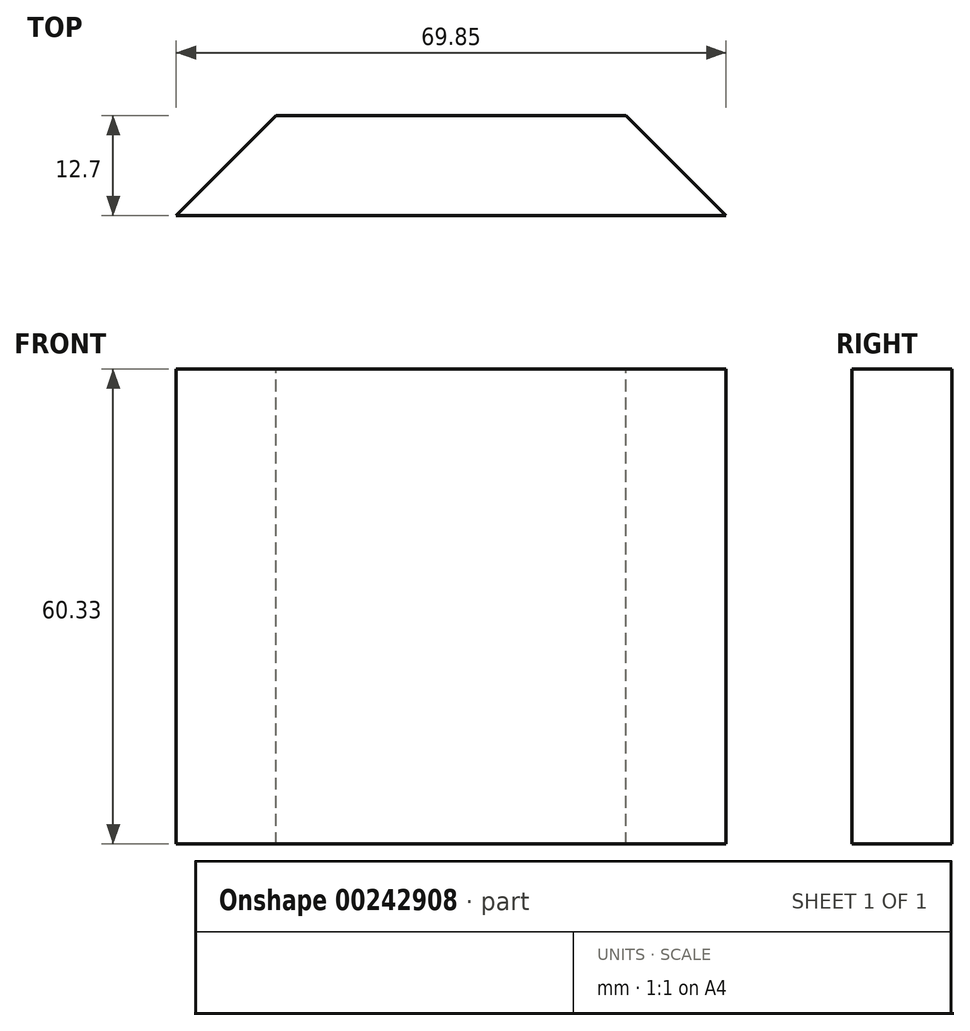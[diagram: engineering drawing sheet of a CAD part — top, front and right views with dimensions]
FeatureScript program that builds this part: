
annotation { "Feature Type Name" : "Feature", "Feature Type Description" : "" }
export const myFeature = defineFeature(function(context is Context, id is Id, definition is map)
    precondition{}
    {
        {
            var Q0;
            Q0=qCreatedBy(makeId("Front.planeOp"),FACE);
            var sketch = newSketch(context, id + "F0", { "sketchPlane" : qUnion([Q0])});
            skLineSegment(sketch, "E0", {"start": v(0, 0) * mm, "end": v(0, 60.33) * mm});
            skLineSegment(sketch, "E1", {"start": v(0, 60.33) * mm, "end": v(69.85, 60.33) * mm});
            skLineSegment(sketch, "E2", {"start": v(69.85, 60.33) * mm, "end": v(69.85, 0) * mm});
            skLineSegment(sketch, "E3", {"start": v(69.85, 0) * mm, "end": v(0, 0) * mm});
            skSolve(sketch);
        }
        {
            var Q0;
            Q0=makeQuery(id+"F0.imprint","IMPRINT",FACE,{"disambiguationData":[TD([[makeQuery(id+"F0.imprint","IMPRINT",EDGE,{"derivedFrom":sQuery(id+"F0.wireOp",EDGE,"E0")}),-1.0]])]});
            extrude(context, id + "F1", {"entities" : qUnion([Q0]), "depth" : 12.7 * mm});
        }
        {
            var Q0;
            Q0=makeQuery(id+"F1.opExtrude","SWEPT_FACE",FACE,{"disambiguationData":[OSD([sQuery(id+"F0.wireOp",EDGE,"E1")])]});
            var sketch = newSketch(context, id + "F2", { "sketchPlane" : qUnion([Q0])});
            skLineSegment(sketch, "E4", {"start": v(0, 0) * mm, "end": v(12.7, 0) * mm});
            skLineSegment(sketch, "E5", {"start": v(12.7, 0) * mm, "end": v(0, -12.7) * mm});
            skLineSegment(sketch, "E6", {"start": v(0, -12.7) * mm, "end": v(0, 0) * mm});
            skLineSegment(sketch, "E7", {"start": v(69.85, 0) * mm, "end": v(57.15, 0) * mm});
            skLineSegment(sketch, "E8", {"start": v(57.15, 0) * mm, "end": v(69.85, -12.7) * mm});
            skLineSegment(sketch, "E9", {"start": v(69.85, -12.7) * mm, "end": v(69.85, 0) * mm});
            skSolve(sketch);
        }
        {
            var Q0;
            Q0=makeQuery(id+"F2.imprint","IMPRINT",FACE,{"disambiguationData":[TD([[makeQuery(id+"F2.imprint","IMPRINT",EDGE,{"derivedFrom":sQuery(id+"F2.wireOp",EDGE,"E4")}),-1.0]])]});
            var Q1;
            Q1=makeQuery(id+"F2.imprint","IMPRINT",FACE,{"disambiguationData":[TD([[makeQuery(id+"F2.imprint","IMPRINT",EDGE,{"derivedFrom":sQuery(id+"F2.wireOp",EDGE,"E7")}),-1.0]])]});
            extrude(context, id + "F3", {"entities" : qUnion([Q0, Q1]), "operationType" : NewBodyOperationType.REMOVE, "oppositeDirection" : true, "depth" : 76.2 * mm});
        }
    });
